# Revit family: VL2P-GL150xWSxxxBU
name_source: partatom
category: Leuchten
units: mm (PartAtom-declared; Revit-internal decimal feet)

## family parameters
Basisbauteil = Fläche
Beim Laden mit Abzugskörper schneiden = Nein
Bemaßung runder Anschluss = Durchmesser verwenden
Beschriftungsausrichtung beibehalten = Nein
Gemeinsam genutzt = Nein
Lichtquelle = Ja
OmniClass-Nummer = 23.80.70.11
OmniClass-Titel = Luminaries for Internal Lighting
Raumberechnungspunkt = Nein
Teiletyp = Normal

## types (13) — shared parameters
Baugruppenkennzeichen = D5020200
Datei für fotometrisches Netz = Master_VLxx-GLxxxBU_IP20.IES
Emissionsform beim Rendern sichtbar = Nein
Farbfilter = 16777215
Farbtemperaturverschiebung bei Dämpfen der Lampe = <Keine Auswahl>
Hersteller = RIDI Leuchten GmbH
Lampe = LED
Neigungswinkel = 90.00°
URL = www.ridi.de
Von Breite des Rechtecks ausssenden = 1480 mm  [stored 4.85564 ft]
Von Länge des Rechtecks aussenden = 61 mm  [stored 0.200131 ft]
brand = RIDI
conformity mark = CE
electrical safety class = 1
height = 64 mm  [stored 0.209974 ft]
ingress protection (IP) code = IP20
length = 1500 mm  [stored 4.92126 ft]
nominal frequency = 50-60Hz
nominal voltage = 230
voltage type (AC, DC, UC) = AC
weight = 1,7kg
width = 67 mm
zero-valued in all types: Vorgabe-Ansicht

## per-type parameters (varying)
| type | Modell | Scheinlast | rated input power |
| VL2P-GL150-5FLWS840BU0650 | 2550039 | 37 VA | 37 |
| VL2P-GL150-7DAWS840BU00650 | 2560039 | 37 VA | 37 |
| VL2P-GL150-5FLWS830BU0650 | 2550186 | 37 VA | 37 |
| VL2P-GL150-7DAWS830BU0650 | 2560186 | 37 VA | 37 |
| VL2P-GL150-5FLWS830BU0800 | 2550187 | 47 VA | 47 |
| VL2P-GL150-7FLWS830BU0650-ED | 2550186//377 | 37 VA | 37 |
| VL2P-GL150-13DAWS830BU0650-ED | 2560186//381 | 37 VA | 37 |
| VL2P-GL150-7FLWS840BU0650-ED | 2550039//377 | 37 VA | 37 |
| VL2P-GL150-7FLWS865BU0650-ED | 2550177//377 | 37 VA | 37 |
| VL2P-GL150-13DAWS840BU0650-ED | 2560039//381 | 37 VA | 37 |
| VL2P-GL150-13DAWS865BU0650-ED | 2560177//377 | 37 VA | 37 |
| VL2P-GL150-7DAWS865BU0650 | 2560177 | 37 VA | 37 |
| VL2P-GL150-5FLWS865BU0650 | 2550177 | 36 VA | 36 |

note: column(s) folded — value = type name in every type: product name

note: [stored X ft] marks values corroborated as IEEE doubles in the binary element streams (Revit-internal decimal feet)
